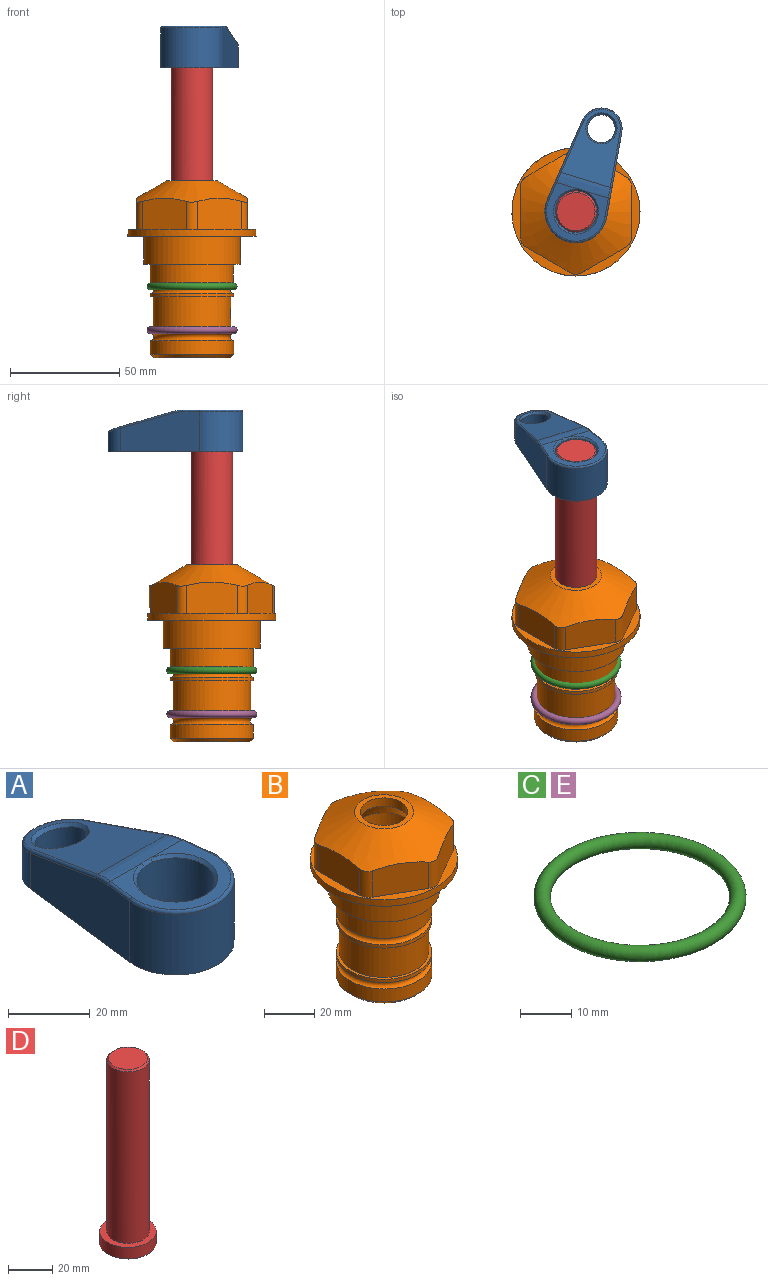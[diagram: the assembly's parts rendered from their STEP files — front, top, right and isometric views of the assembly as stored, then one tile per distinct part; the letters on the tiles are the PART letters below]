
ASSEMBLY  parts=5 mates=4
PART A: 31 faces, bbox 31.7x65.5x19.8 mm
  f0: plane 39.12x18.26mm, normal (0.99,0.12,0), area 612.2mm2, adj f1,f4,f7,f11,f13,f15
  f1: cylinder r=9.53mm len=18.91mm, axis (0,0,-1), area 296.1mm2, adj f0,f2,f7,f17
  f2: plane 39.12x18.26mm, normal (-0.99,0.12,0), area 612.2mm2, adj f1,f4,f7,f12,f14,f16
  f3: cylinder r=6.35mm len=12.7mm, axis (0,0,-1), area 362.4mm2, adj f7,f18
  f4: cylinder r=14.29mm len=28.58mm, axis (0,0,-1), area 882.2mm2, adj f0,f2,f7,f10
  f5: cylinder r=9.53mm len=19.05mm, axis (0,0,-1), area 1092.6mm2, adj f7,f19,f20
  f6: plane 26.99x23.69mm, normal (0,0,1), area 216.2mm2, adj f9,f10,f11,f12,f19
  f7: plane 63.5x28.58mm, normal (0,0,-1), area 661.8mm2, adj f0,f1,f2,f3,f4,f5,f22,f23
  f8: plane 33.52x23.6mm, normal (0,0.26,0.97), area 486mm2, adj f9,f15,f16,f17,f18
  f9: cylinder r=19.05mm len=24.72mm, axis (1,0,0), area 120.4mm2, adj f6,f8,f13,f14,f20
  f10: torus R=13.49mm, axis (0,0,1), area 59mm2, adj f4,f6,f11,f12
  f11: cylinder r=0.79mm len=8.67mm, axis (0.12,-0.99,0), area 10.8mm2, adj f0,f6,f10,f13
  f12: cylinder r=0.79mm len=8.67mm, axis (0.12,0.99,0), area 10.8mm2, adj f2,f6,f10,f14
  f13: bspline ~4.95x1.42mm, area 6.1mm2, adj f0,f9,f11,f15
  f14: bspline ~4.95x1.42mm, area 6.1mm2, adj f2,f9,f12,f16
  f15: cylinder r=0.79mm len=25.95mm, axis (0.12,-0.96,0.26), area 32.9mm2, adj f0,f8,f13,f17
  f16: cylinder r=0.79mm len=25.95mm, axis (0.12,0.96,-0.26), area 32.9mm2, adj f2,f8,f14,f17
  f17: bspline ~18.91x8.38mm, area 30mm2, adj f1,f8,f15,f16
  f18: bspline ~14.29x14.29mm, area 48.3mm2, adj f3,f8
  f19: cone r=9.53mm half-angle=45deg, axis (0,0,1), area 66.5mm2, adj f5,f6,f20
  f20: bspline ~3.22x0.96mm, area 3.5mm2, adj f5,f9,f19
  f21: plane 2.75x2.72mm, normal (0,0,-1), area 2.9mm2, adj f23,f25,f28
  f22: plane 23.05x15.88mm, normal (-0.99,-0.12,0), area 323.6mm2, adj f7,f25,f26,f27,f28,f29
  f23: plane 23.05x15.88mm, normal (0.99,-0.12,0), area 323.6mm2, adj f7,f21,f25,f27,f28,f30
  f24: cylinder r=9.53mm len=10.69mm, axis (0,0,-1), area 114.7mm2, adj f7,f27,f29,f30
  f25: cylinder r=12.7mm len=20.59mm, axis (0,0,-1), area 381.1mm2, adj f7,f21,f22,f23,f26,f28
  f26: plane 2.75x2.72mm, normal (0,0,-1), area 2.9mm2, adj f22,f25,f28
  f27: plane 19.72x18.37mm, normal (0,-0.26,-0.97), area 291.8mm2, adj f22,f23,f24,f28,f29,f30
  f28: cylinder r=15.88mm len=19.92mm, axis (1,0,0), area 54.8mm2, adj f21,f22,f23,f25,f26,f27
  f29: cylinder r=1.59mm len=11mm, axis (0,0,-1), area 34.7mm2, adj f7,f22,f24,f27
  f30: cylinder r=1.59mm len=11mm, axis (0,0,-1), area 34.7mm2, adj f7,f23,f24,f27
PART B: 36 faces, bbox 58.7x58.7x81 mm
  f0: cylinder r=17.78mm len=35.56mm, axis (0,0,1), area 1670.8mm2, adj f23,f24,f31
  f1: cylinder r=19.05mm len=38.1mm, axis (0,0,1), area 1191.9mm2, adj f26,f27,f30
  f2: plane 58.66x58.66mm, normal (0,0,-1), area 1150.6mm2, adj f3,f28
  f3: cylinder r=29.33mm len=58.66mm, axis (0,0,-1), area 585.1mm2, adj f2,f4
  f4: plane 58.66x58.66mm, normal (0,0,1), area 475.9mm2, adj f3,f5,f6,f7,f8,f9,f10,f11
  f5: plane 20.32x14.34mm, normal (-0.5,0.87,0), area 324.4mm2, adj f4,f15,f16,f17
  f6: plane 20.32x14.34mm, normal (0.5,0.87,0), area 324.4mm2, adj f4,f14,f15,f17
  f7: plane 23.48x14.34mm, normal (1,0,0), area 324.4mm2, adj f4,f13,f14,f17
  f8: plane 20.32x14.34mm, normal (0.5,-0.87,0), area 324.4mm2, adj f4,f12,f13,f17
  f9: plane 20.32x14.34mm, normal (-0.5,-0.87,0), area 324.4mm2, adj f4,f11,f12,f17
  f10: plane 23.48x14.34mm, normal (-1,0,0), area 324.4mm2, adj f4,f11,f16,f17
  f11: cylinder r=5.08mm len=12.85mm, axis (0,0,-1), area 67.2mm2, adj f4,f9,f10,f17
  f12: cylinder r=5.08mm len=12.85mm, axis (0,0,-1), area 67.2mm2, adj f4,f8,f9,f17
  f13: cylinder r=5.08mm len=12.85mm, axis (0,0,-1), area 67.2mm2, adj f4,f7,f8,f17
  f14: cylinder r=5.08mm len=12.85mm, axis (0,0,-1), area 67.2mm2, adj f4,f6,f7,f17
  f15: cylinder r=5.08mm len=12.85mm, axis (0,0,-1), area 67.2mm2, adj f4,f5,f6,f17
  f16: cylinder r=5.08mm len=12.85mm, axis (0,0,-1), area 67.2mm2, adj f4,f5,f10,f17
  f17: cone r=11.73mm half-angle=60deg, axis (0,0,-1), area 2071.8mm2, adj f5,f6,f7,f8,f9,f10,f11,f12
  f18: plane 23.46x23.46mm, normal (0,0,1), area 147.4mm2, adj f17,f35
  f19: plane 34.93x34.93mm, normal (0,0,-1), area 958mm2, adj f29
  f20: cylinder r=19.05mm len=38.1mm, axis (0,0,1), area 760.1mm2, adj f21,f29
  f21: torus R=19.05mm, axis (0,0,1), area 565.3mm2, adj f20,f22
  f22: cylinder r=19.05mm len=38.1mm, axis (0,0,1), area 190mm2, adj f21,f23
  f23: plane 38.1x38.1mm, normal (0,0,1), area 146.9mm2, adj f0,f22
  f24: plane 38.1x38.1mm, normal (0,0,-1), area 146.9mm2, adj f0,f25
  f25: cylinder r=19.05mm len=38.1mm, axis (0,0,1), area 190mm2, adj f24,f26
  f26: torus R=19.05mm, axis (0,0,1), area 565.3mm2, adj f1,f25
  f27: plane 44.45x44.45mm, normal (0,0,-1), area 411.7mm2, adj f1,f28
  f28: cylinder r=22.23mm len=44.45mm, axis (0,0,1), area 1773.5mm2, adj f2,f27
  f29: cone r=19.05mm half-angle=45deg, axis (0,0,1), area 257.5mm2, adj f19,f20
  f30: cylinder r=3.17mm len=6.75mm, axis (-1,0,0), area 128mm2, adj f1,f33
  f31: cylinder r=3.17mm len=6.35mm, axis (-1,0,0), area 102.5mm2, adj f0,f33
  f32: plane 25.4x25.4mm, normal (0,0,1), area 506.7mm2, adj f33
  f33: cylinder r=12.7mm len=66.42mm, axis (0,0,-1), area 5236.2mm2, adj f30,f31,f32,f34
  f34: cone r=9.53mm half-angle=30deg, axis (0,0,-1), area 443.4mm2, adj f33,f35
  f35: cylinder r=9.53mm len=19.05mm, axis (0,0,-1), area 240.9mm2, adj f18,f34
PART C: 1 faces, bbox 44.7x44.7x3.2 mm
  f0: torus R=19.05mm, axis (0,0,1), area 1193.9mm2
PART D: 6 faces, bbox 25.4x25.4x101.6 mm
  f0: plane 17.46x17.46mm, normal (0,0,1), area 239.5mm2, adj f5
  f1: plane 25.4x25.4mm, normal (0,0,-1), area 506.7mm2, adj f2
  f2: cylinder r=12.7mm len=25.4mm, axis (0,0,1), area 506.7mm2, adj f1,f3
  f3: plane 25.4x25.4mm, normal (0,0,1), area 221.7mm2, adj f2,f4
  f4: cylinder r=9.53mm len=94.46mm, axis (0,0,1), area 5653mm2, adj f3,f5
  f5: cone r=8.73mm half-angle=45deg, axis (0,0,-1), area 64.4mm2, adj f0,f4
PART E: same geometry as C
PLACE A rot(axis=(0,0,-1),17deg) t=(0,0,32.79)mm
PLACE B at identity fixed
PLACE C t=(0,0,1.59)mm
PLACE D rot(axis=(0,0,-1),17deg) t=(0,0,32)mm
PLACE E t=(0,0,-18.41)mm
MATE fastened C.f0 <-> B.f0  axis (0,0,1) through (0,0,-22.92)mm
MATE fastened A.f4 <-> D.f2  axis (0,0,-1) through (0,0,95.5)mm
MATE cylindrical B.f0 <-> D.f2  axis (0,0,1) through (0,0,-42.93)mm
MATE fastened E.f0 <-> B.f0  axis (0,0,1) through (0,0,-42.93)mm
